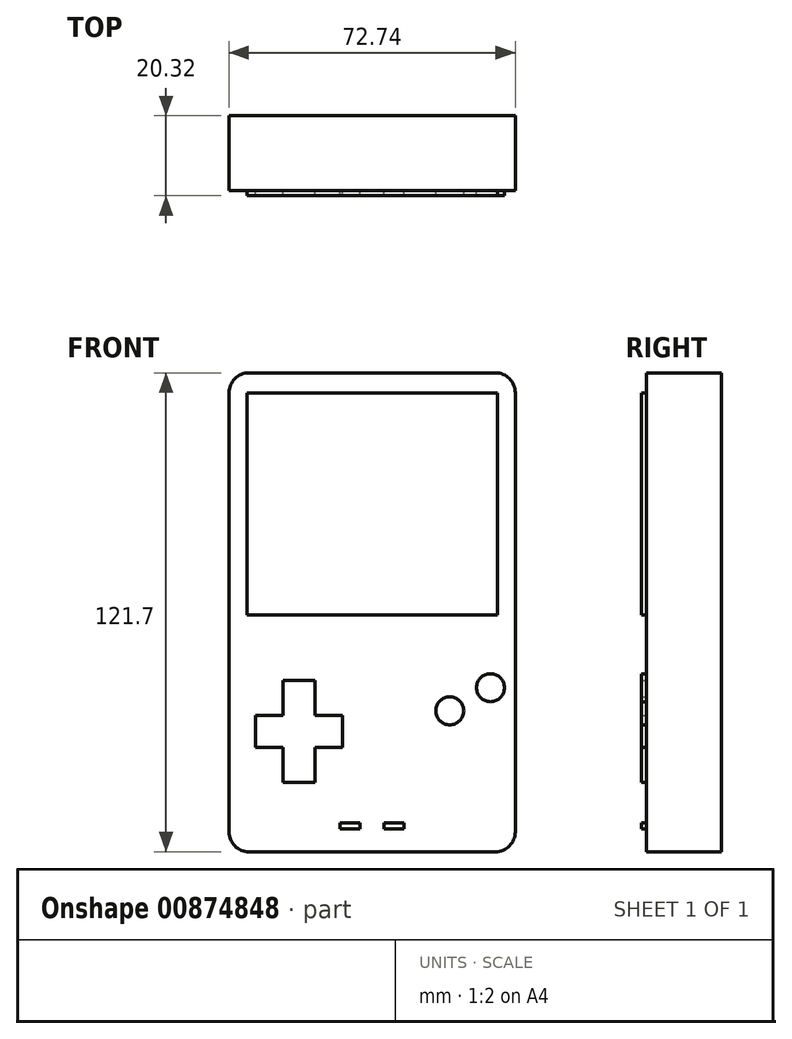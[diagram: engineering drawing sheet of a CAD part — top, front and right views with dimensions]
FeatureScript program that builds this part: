
annotation { "Feature Type Name" : "Feature", "Feature Type Description" : "" }
export const myFeature = defineFeature(function(context is Context, id is Id, definition is map)
    precondition{}
    {
        {
            var Q0;
            Q0=qCreatedBy(makeId("Front.planeOp"),FACE);
            var sketch = newSketch(context, id + "F0", { "sketchPlane" : qUnion([Q0])});
            skLineSegment(sketch, "E0.bottom", {"start": v(-36.37, 60.85) * mm, "end": v(36.37, 60.85) * mm});
            skLineSegment(sketch, "E0.top", {"start": v(-36.37, -60.85) * mm, "end": v(36.37, -60.85) * mm});
            skLineSegment(sketch, "E0.left", {"start": v(-36.37, 60.85) * mm, "end": v(-36.37, -60.85) * mm});
            skLineSegment(sketch, "E0.right", {"start": v(36.37, 60.85) * mm, "end": v(36.37, -60.85) * mm});
            skLineSegment(sketch, "E1", {"start": v(0, 60.85) * mm, "end": v(0, -60.85) * mm, "construction": true});
            skSolve(sketch);
        }
        {
            var Q0;
            Q0 = qSketchRegion(id + "F0", true);
            extrude(context, id + "F1", {"entities" : qUnion([Q0]), "depth" : 19.05 * mm, "offsetDistance" : 25.4 * mm});
        }
        {
            var Q0;
            Q0=makeQuery(id+"F1.opExtrude","CAP_FACE",FACE,{"disambiguationData":[OSD([sQuery(id+"F0.wireOp",EDGE,"E0.bottom"),sQuery(id+"F0.wireOp",EDGE,"E0.top"),sQuery(id+"F0.wireOp",EDGE,"E0.left"),sQuery(id+"F0.wireOp",EDGE,"E0.right")])],"isStart":false});
            var sketch = newSketch(context, id + "F2", { "sketchPlane" : qUnion([Q0])});
            skLineSegment(sketch, "E2.bottom", {"start": v(-31.8, 55.77) * mm, "end": v(31.8, 55.77) * mm});
            skLineSegment(sketch, "E2.top", {"start": v(-31.8, -0.68) * mm, "end": v(31.8, -0.68) * mm});
            skLineSegment(sketch, "E2.left", {"start": v(-31.8, 55.77) * mm, "end": v(-31.8, -0.68) * mm});
            skLineSegment(sketch, "E2.right", {"start": v(31.8, 55.77) * mm, "end": v(31.8, -0.68) * mm});
            skLineSegment(sketch, "E3", {"start": v(-22.63, -17.31) * mm, "end": v(-14.5, -17.31) * mm});
            skLineSegment(sketch, "E4", {"start": v(-14.5, -17.31) * mm, "end": v(-14.5, -26.2) * mm});
            skLineSegment(sketch, "E5", {"start": v(-14.5, -26.2) * mm, "end": v(-7.52, -26.2) * mm});
            skLineSegment(sketch, "E6", {"start": v(-7.52, -26.2) * mm, "end": v(-7.52, -34.33) * mm});
            skLineSegment(sketch, "E7", {"start": v(-7.52, -34.33) * mm, "end": v(-14.5, -34.33) * mm});
            skLineSegment(sketch, "E8", {"start": v(-14.5, -34.33) * mm, "end": v(-14.5, -43.22) * mm});
            skLineSegment(sketch, "E9", {"start": v(-14.5, -43.22) * mm, "end": v(-22.63, -43.22) * mm});
            skLineSegment(sketch, "E10", {"start": v(-22.63, -43.22) * mm, "end": v(-22.63, -34.33) * mm});
            skLineSegment(sketch, "E11", {"start": v(-22.63, -34.33) * mm, "end": v(-29.61, -34.33) * mm});
            skLineSegment(sketch, "E12", {"start": v(-29.61, -34.33) * mm, "end": v(-29.61, -26.2) * mm});
            skLineSegment(sketch, "E13", {"start": v(-29.61, -26.2) * mm, "end": v(-22.62, -26.2) * mm});
            skLineSegment(sketch, "E14", {"start": v(-22.62, -26.2) * mm, "end": v(-22.62, -17.31) * mm});
            skCircle(sketch, "E15", {"center": v(30.07, -19.16) * mm, "radius": 3.56 * mm});
            skCircle(sketch, "E16", {"center": v(19.72, -25.04) * mm, "radius": 3.56 * mm});
            skLineSegment(sketch, "E17.bottom", {"start": v(-8.13, -53.5) * mm, "end": v(-3.05, -53.5) * mm});
            skLineSegment(sketch, "E17.top", {"start": v(-8.13, -55.03) * mm, "end": v(-3.05, -55.03) * mm});
            skLineSegment(sketch, "E17.left", {"start": v(-8.13, -53.5) * mm, "end": v(-8.13, -55.03) * mm});
            skLineSegment(sketch, "E17.right", {"start": v(-3.05, -53.5) * mm, "end": v(-3.05, -55.03) * mm});
            skLineSegment(sketch, "E18", {"start": v(0, -56.36) * mm, "end": v(0, -51.19) * mm});
            skLineSegment(sketch, "E19.MirrorCS", {"start": v(8.13, -53.5) * mm, "end": v(3.05, -53.5) * mm});
            skLineSegment(sketch, "E20.MirrorCS", {"start": v(3.05, -53.5) * mm, "end": v(3.05, -55.03) * mm});
            skLineSegment(sketch, "E21.MirrorCS", {"start": v(8.13, -55.03) * mm, "end": v(3.05, -55.03) * mm});
            skLineSegment(sketch, "E22.MirrorCS", {"start": v(8.13, -53.5) * mm, "end": v(8.13, -55.03) * mm});
            skSolve(sketch);
        }
        {
            var Q0;
            Q0 = qSketchRegion(id + "F2", true);
            extrude(context, id + "F3", {"entities" : qUnion([Q0]), "operationType" : NewBodyOperationType.ADD, "depth" : 1.27 * mm, "offsetDistance" : 25.4 * mm});
        }
        {
            var Q0;
            Q0=makeQuery(id+"F1.opExtrude","SWEPT_EDGE",EDGE,{"disambiguationData":[OSD([sQuery(id+"F0.wireOp",EDGE,"E0.bottom"),sQuery(id+"F0.wireOp",EDGE,"E0.left")])]});
            var Q1;
            Q1=makeQuery(id+"F1.opExtrude","SWEPT_EDGE",EDGE,{"disambiguationData":[OSD([sQuery(id+"F0.wireOp",EDGE,"E0.bottom"),sQuery(id+"F0.wireOp",EDGE,"E0.right")])]});
            var Q2;
            Q2=makeQuery(id+"F1.opExtrude","SWEPT_EDGE",EDGE,{"disambiguationData":[OSD([sQuery(id+"F0.wireOp",EDGE,"E0.top"),sQuery(id+"F0.wireOp",EDGE,"E0.right")])]});
            var Q3;
            Q3=makeQuery(id+"F1.opExtrude","SWEPT_EDGE",EDGE,{"disambiguationData":[OSD([sQuery(id+"F0.wireOp",EDGE,"E0.top"),sQuery(id+"F0.wireOp",EDGE,"E0.left")])]});
            fillet(context, id + "F4", {"entities" : qUnion([Q0, Q1, Q2, Q3]), "radius" : 5.08 * mm, "tangentPropagation" : true, "allowEdgeOverflow" : false});
        }
    });
